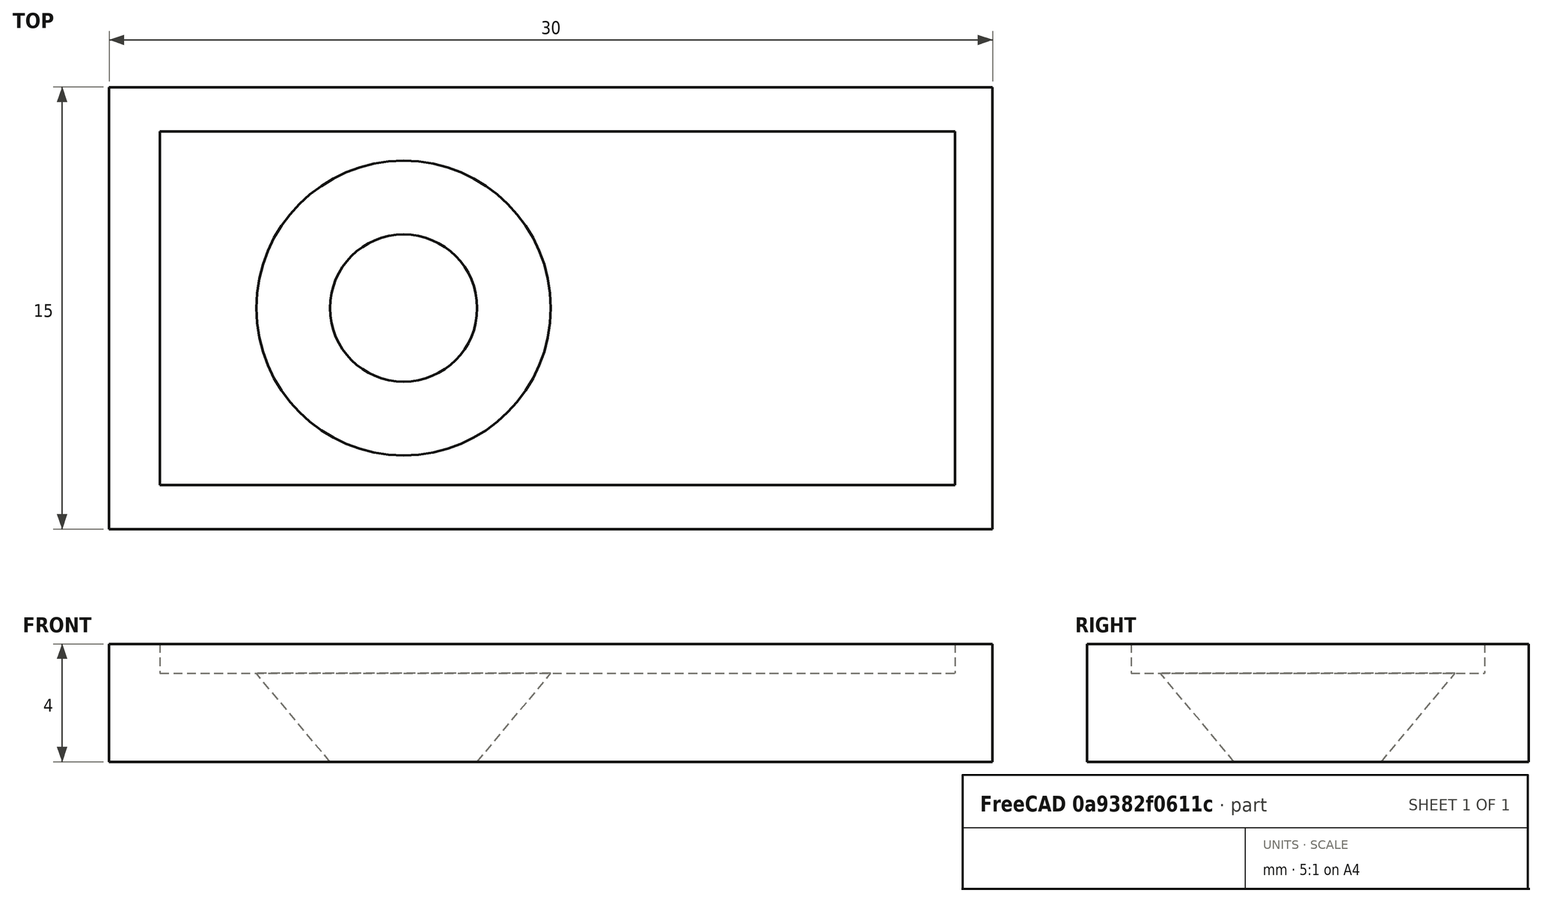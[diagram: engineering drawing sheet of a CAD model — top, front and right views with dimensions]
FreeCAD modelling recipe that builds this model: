
FCSTD DOCUMENT  (FreeCAD 0.18.3R)
Label: lamp.base.leg
License: All rights reserved
LicenseURL: http://en.wikipedia.org/wiki/All_rights_reserved
objects: Part::Part2DObjectPython×3, Part::Extrusion×3, Part::Cut×3, Part::Cone×1
note: 10 computed .brp shape members not serialized (recipe doc carries the construction recipe); baked Part::Feature solids carry a one-line shape summary decoded from their .brp

FEATURE [Part::Part2DObjectPython] Rectangle  # Draft 2D object (typed FeaturePython)
  ChamferSize = 0
  Columns = 1
  FilletRadius = 0
  Height = 15
  Length = 30
  MakeFace = true
  Placement = pos=(-3.07351,-3.08139,0) rot=(0,0,1;0rad)
  Rows = 1
FEATURE [Part::Extrusion] Extrude
  Base = -> Rectangle
  Dir = (0,0,1)
  DirMode = 2
  FaceMakerClass = Part::FaceMakerBullseye
  LengthFwd = 4
  LengthRev = 0
  Solid = false
  Symmetric = false
FEATURE [Part::Part2DObjectPython] Circle  # Draft 2D object (typed FeaturePython)
  FirstAngle = 0
  LastAngle = 0
  MakeFace = true
  Placement = pos=(6.92649,4.41861,0) rot=(0,0,1;0rad)
  Radius = 2.5
FEATURE [Part::Extrusion] Extrude001
  Base = -> Circle
  Dir = (0,0,1)
  DirMode = 2
  FaceMakerClass = Part::FaceMakerBullseye
  LengthFwd = 10
  LengthRev = 0
  Solid = false
  Symmetric = false
FEATURE [Part::Cone] Cone
  Angle = 360
  AttacherType = Attacher::AttachEngine3D
  Height = 3
  Placement = pos=(6.92649,4.41861,0) rot=(0,0,1;0rad)
  Radius1 = 2.5
  Radius2 = 5
FEATURE [Part::Cut] Cut
  Base = -> Extrude
  Tool = -> Extrude001
FEATURE [Part::Part2DObjectPython] Rectangle001  # Draft 2D object (typed FeaturePython)
  ChamferSize = 0
  Columns = 1
  FilletRadius = 0
  Height = 12
  Length = 27
  MakeFace = true
  Placement = pos=(-1.34539,-1.58139,4) rot=(0,0,1;0rad)
  Rows = 1
FEATURE [Part::Cut] Cut001
  Base = -> Cut
  Tool = -> Cone
FEATURE [Part::Extrusion] Extrude002
  Base = -> Rectangle001
  Dir = (0,0,1)
  DirMode = 2
  FaceMakerClass = Part::FaceMakerBullseye
  LengthFwd = -1
  LengthRev = 0
  Solid = false
  Symmetric = false
FEATURE [Part::Cut] Cut002
  Base = -> Cut001
  Tool = -> Extrude002
